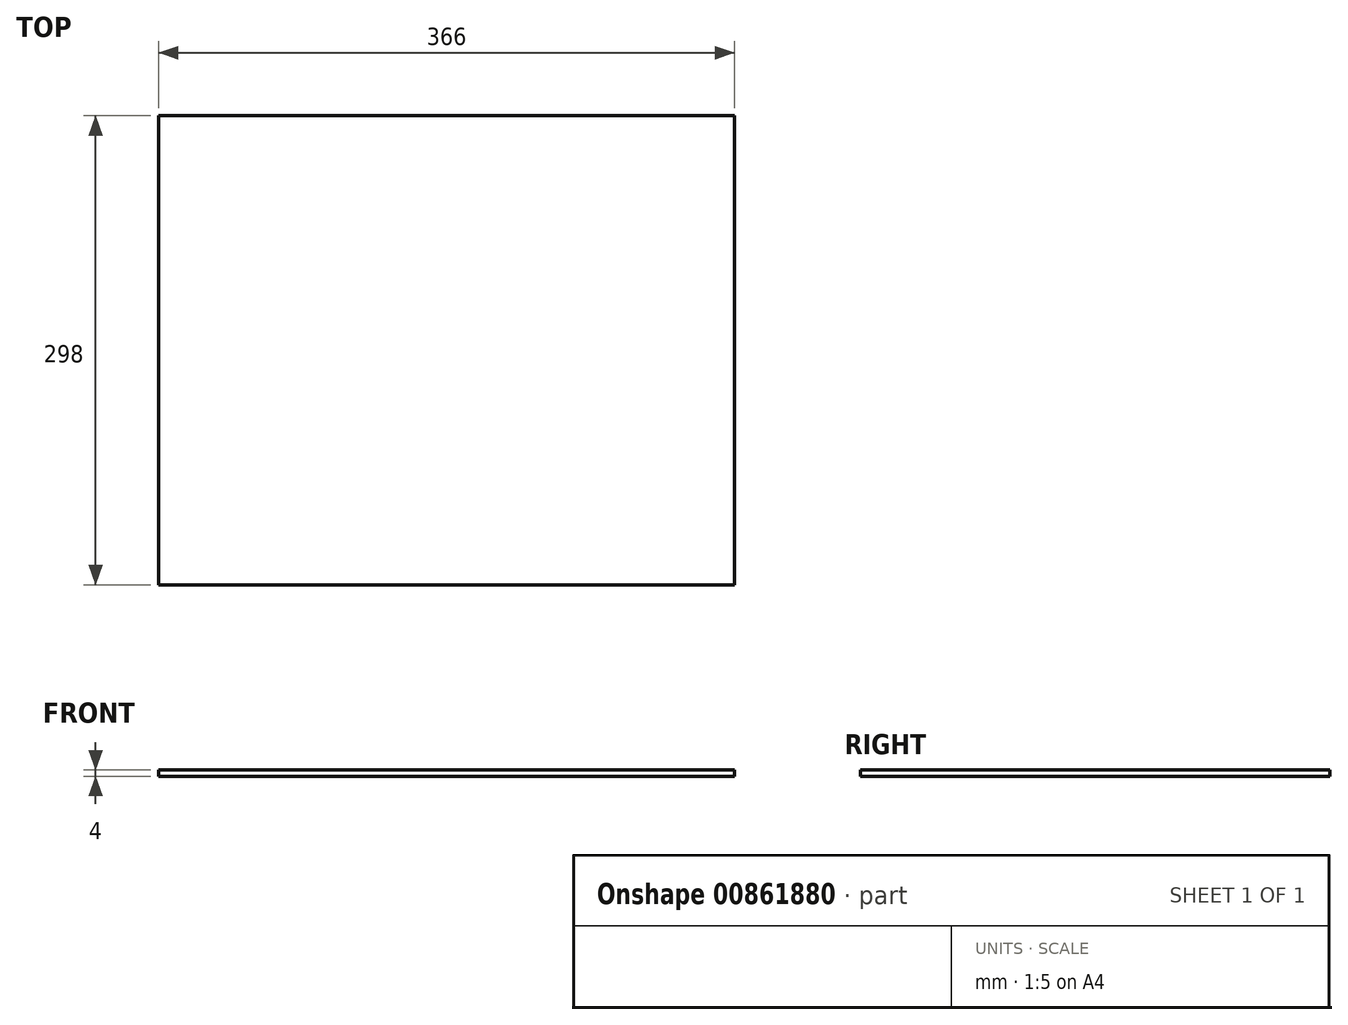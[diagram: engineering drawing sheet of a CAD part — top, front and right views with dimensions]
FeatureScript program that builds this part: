
annotation { "Feature Type Name" : "Feature", "Feature Type Description" : "" }
export const myFeature = defineFeature(function(context is Context, id is Id, definition is map)
    precondition{}
    {
        {
            var Q0;
            Q0=qCreatedBy(makeId("Top.planeOp"),FACE);
            var sketch = newSketch(context, id + "F0", { "sketchPlane" : qUnion([Q0])});
            skLineSegment(sketch, "E0.bottom", {"start": v(-183, -149) * mm, "end": v(183, -149) * mm});
            skLineSegment(sketch, "E0.top", {"start": v(-183, 149) * mm, "end": v(183, 149) * mm});
            skLineSegment(sketch, "E0.left", {"start": v(-183, -149) * mm, "end": v(-183, 149) * mm});
            skLineSegment(sketch, "E0.right", {"start": v(183, -149) * mm, "end": v(183, 149) * mm});
            skPoint(sketch, "E0.middle", {"position": v(0, 0) * mm});
            skSolve(sketch);
        }
        {
            var Q0;
            Q0=makeQuery(id+"F0.imprint","IMPRINT",FACE,{"disambiguationData":[TD([[makeQuery(id+"F0.imprint","IMPRINT",EDGE,{"derivedFrom":sQuery(id+"F0.wireOp",EDGE,"E0.bottom")}),1.0]])]});
            extrude(context, id + "F1", {"entities" : qUnion([Q0]), "depth" : 4 * mm, "offsetDistance" : 25 * mm});
        }
    });
